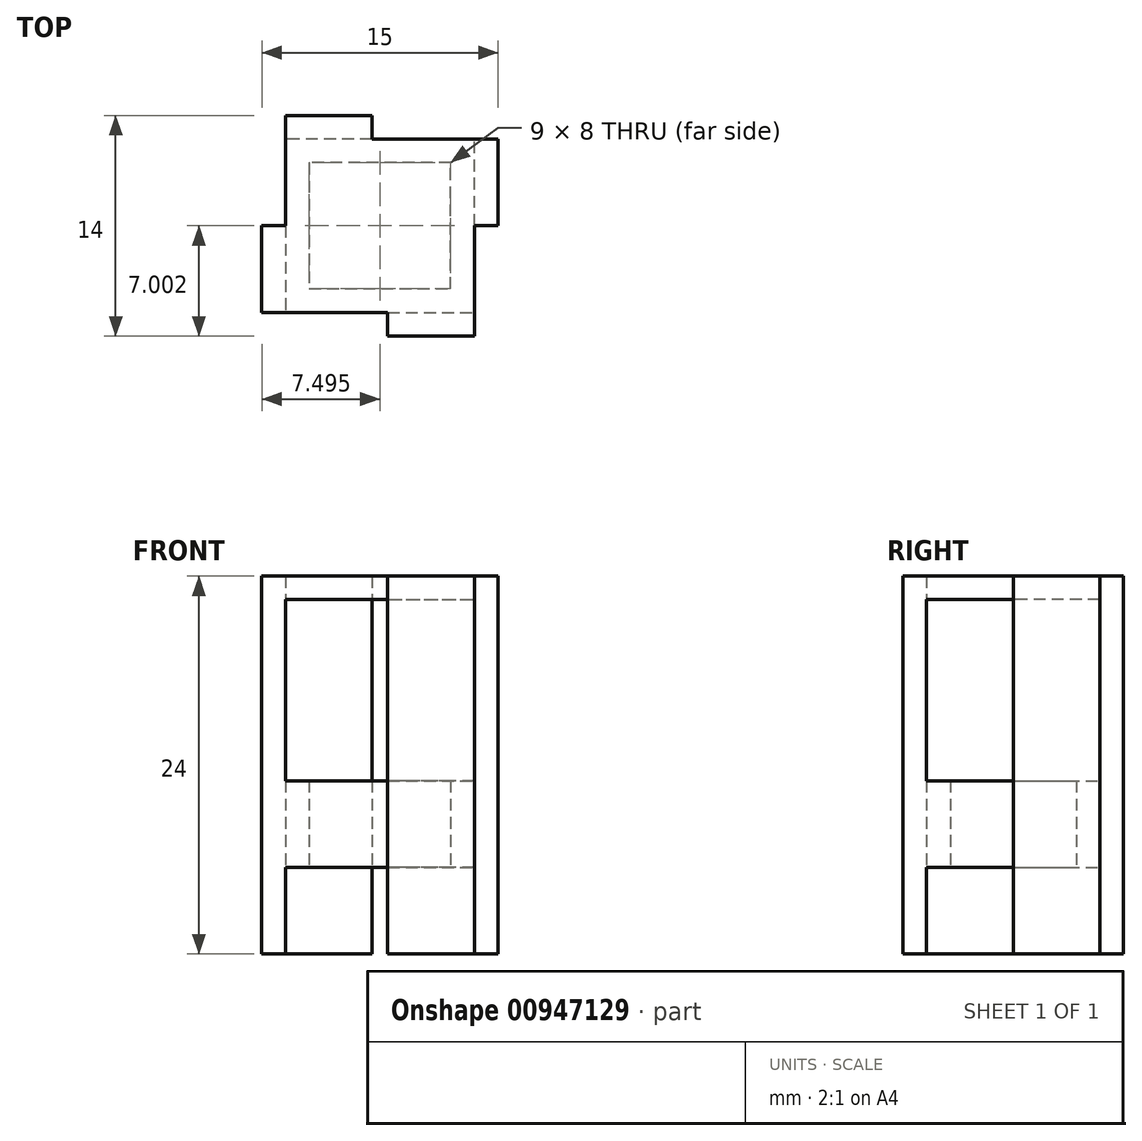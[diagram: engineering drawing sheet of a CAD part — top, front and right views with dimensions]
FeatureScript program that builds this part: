
annotation { "Feature Type Name" : "Feature", "Feature Type Description" : "" }
export const myFeature = defineFeature(function(context is Context, id is Id, definition is map)
    precondition{}
    {
        {
            var Q0;
            Q0=qCreatedBy(makeId("Top.planeOp"),FACE);
            var sketch = newSketch(context, id + "F0", { "sketchPlane" : qUnion([Q0])});
            skLineSegment(sketch, "E0.bottom", {"start": v(8.63, 13.95) * mm, "end": v(20.63, 13.95) * mm});
            skLineSegment(sketch, "E0.top", {"start": v(8.63, 8.45) * mm, "end": v(20.63, 8.45) * mm});
            skLineSegment(sketch, "E0.left", {"start": v(8.63, 13.95) * mm, "end": v(8.63, 8.45) * mm});
            skLineSegment(sketch, "E0.right", {"start": v(20.63, 13.95) * mm, "end": v(20.63, 8.45) * mm});
            skLineSegment(sketch, "E1.top", {"start": v(8.63, 2.95) * mm, "end": v(20.63, 2.95) * mm});
            skLineSegment(sketch, "E1.left", {"start": v(8.63, 8.45) * mm, "end": v(8.63, 2.95) * mm});
            skLineSegment(sketch, "E1.right", {"start": v(20.63, 8.45) * mm, "end": v(20.63, 2.95) * mm});
            skSolve(sketch);
        }
        {
            var Q0;
            Q0 = qSketchRegion(id + "F0", true);
            extrude(context, id + "F1", {"entities" : qUnion([Q0]), "depth" : 1.5 * mm, "offsetDistance" : 25 * mm});
        }
        {
            var Q0;
            Q0=makeQuery(id+"F1.opExtrude","SWEPT_FACE",FACE,{"disambiguationData":[OSD([sQuery(id+"F0.wireOp",EDGE,"E1.top")])]});
            var sketch = newSketch(context, id + "F2", { "sketchPlane" : qUnion([Q0])});
            skLineSegment(sketch, "E2.bottom", {"start": v(20.63, 1.5) * mm, "end": v(15.13, 1.5) * mm});
            skLineSegment(sketch, "E2.top", {"start": v(20.63, -22.5) * mm, "end": v(15.13, -22.5) * mm});
            skLineSegment(sketch, "E2.left", {"start": v(20.63, 1.5) * mm, "end": v(20.63, -22.5) * mm});
            skLineSegment(sketch, "E2.right", {"start": v(15.13, 1.5) * mm, "end": v(15.13, -22.5) * mm});
            skSolve(sketch);
        }
        {
            var Q0;
            Q0 = qSketchRegion(id + "F2", true);
            extrude(context, id + "F3", {"entities" : qUnion([Q0]), "operationType" : NewBodyOperationType.ADD, "depth" : 1.5 * mm, "offsetDistance" : 25 * mm});
        }
        {
            var Q0;
            Q0=makeQuery(id+"F1.opExtrude","SWEPT_FACE",FACE,{"disambiguationData":[OSD([sQuery(id+"F0.wireOp",EDGE,"E0.left"),sQuery(id+"F0.wireOp",EDGE,"E1.left")])]});
            var sketch = newSketch(context, id + "F4", { "sketchPlane" : qUnion([Q0])});
            skLineSegment(sketch, "E3.bottom", {"start": v(-2.95, 1.5) * mm, "end": v(-8.45, 1.5) * mm});
            skLineSegment(sketch, "E3.top", {"start": v(-2.95, -22.5) * mm, "end": v(-8.45, -22.5) * mm});
            skLineSegment(sketch, "E3.left", {"start": v(-2.95, 1.5) * mm, "end": v(-2.95, -22.5) * mm});
            skLineSegment(sketch, "E3.right", {"start": v(-8.45, 1.5) * mm, "end": v(-8.45, -22.5) * mm});
            skSolve(sketch);
        }
        {
            var Q0;
            {var subQ0=sQuery(id+"F4.wireOp",EDGE,"E3.top");Q0=makeQuery(id+"F4.imprint","IMPRINT",FACE,{"disambiguationData":[TD([[makeQuery(id+"F4.imprint","IMPRINT",EDGE,{"derivedFrom":subQ0}),-1.0]])]});}
            var Q1;
            {var subQ0=sQuery(id+"F4.wireOp",EDGE,"E3.bottom");Q1=makeQuery(id+"F4.imprint","IMPRINT",FACE,{"disambiguationData":[TD([[makeQuery(id+"F4.imprint","IMPRINT",EDGE,{"derivedFrom":subQ0}),-1.0]])]});}
            extrude(context, id + "F5", {"entities" : qUnion([Q0, Q1]), "operationType" : NewBodyOperationType.ADD, "depth" : 1.5 * mm, "offsetDistance" : 25 * mm});
        }
        {
            var Q0;
            Q0=makeQuery(id+"F1.opExtrude","SWEPT_FACE",FACE,{"disambiguationData":[OSD([sQuery(id+"F0.wireOp",EDGE,"E0.bottom")])]});
            var sketch = newSketch(context, id + "F6", { "sketchPlane" : qUnion([Q0])});
            skLineSegment(sketch, "E4.bottom", {"start": v(-8.63, 1.5) * mm, "end": v(-14.13, 1.5) * mm});
            skLineSegment(sketch, "E4.top", {"start": v(-8.63, -22.5) * mm, "end": v(-14.13, -22.5) * mm});
            skLineSegment(sketch, "E4.left", {"start": v(-8.63, 1.5) * mm, "end": v(-8.63, -22.5) * mm});
            skLineSegment(sketch, "E4.right", {"start": v(-14.13, 1.5) * mm, "end": v(-14.13, -22.5) * mm});
            skSolve(sketch);
        }
        {
            var Q0;
            Q0 = qSketchRegion(id + "F6", true);
            extrude(context, id + "F7", {"entities" : qUnion([Q0]), "operationType" : NewBodyOperationType.ADD, "depth" : 1.5 * mm, "offsetDistance" : 25 * mm});
        }
        {
            var Q0;
            Q0=makeQuery(id+"F3.boolean.opBoolean","MERGE",FACE,{"derivedFrom":[makeQuery(id+"F1.opExtrude","SWEPT_FACE",FACE,{"disambiguationData":[OSD([sQuery(id+"F0.wireOp",EDGE,"E0.right"),sQuery(id+"F0.wireOp",EDGE,"E1.right")])]}),makeQuery(id+"F3.opExtrude","SWEPT_FACE",FACE,{"disambiguationData":[OSD([sQuery(id+"F2.wireOp",EDGE,"E2.left")])]})]});
            var sketch = newSketch(context, id + "F8", { "sketchPlane" : qUnion([Q0])});
            skLineSegment(sketch, "E5.bottom", {"start": v(13.95, 1.5) * mm, "end": v(8.45, 1.5) * mm});
            skLineSegment(sketch, "E5.top", {"start": v(13.95, -22.5) * mm, "end": v(8.45, -22.5) * mm});
            skLineSegment(sketch, "E5.left", {"start": v(13.95, 1.5) * mm, "end": v(13.95, -22.5) * mm});
            skLineSegment(sketch, "E5.right", {"start": v(8.45, 1.5) * mm, "end": v(8.45, -22.5) * mm});
            skSolve(sketch);
        }
        {
            var Q0;
            Q0 = qSketchRegion(id + "F8", true);
            extrude(context, id + "F9", {"entities" : qUnion([Q0]), "operationType" : NewBodyOperationType.ADD, "depth" : 1.5 * mm, "offsetDistance" : 25 * mm});
        }
        {
            var Q0;
            Q0=makeQuery(id+"F7.boolean.opBoolean","MERGE",FACE,{"derivedFrom":[makeQuery(id+"F1.opExtrude","SWEPT_FACE",FACE,{"disambiguationData":[OSD([sQuery(id+"F0.wireOp",EDGE,"E0.left"),sQuery(id+"F0.wireOp",EDGE,"E1.left")])]}),makeQuery(id+"F7.opExtrude","SWEPT_FACE",FACE,{"disambiguationData":[OSD([sQuery(id+"F6.wireOp",EDGE,"E4.left")])]})]});
            var sketch = newSketch(context, id + "F10", { "sketchPlane" : qUnion([Q0])});
            skLineSegment(sketch, "E6.bottom", {"start": v(-13.95, -11.5) * mm, "end": v(-4.45, -11.5) * mm});
            skLineSegment(sketch, "E6.top", {"start": v(-13.95, -17) * mm, "end": v(-4.45, -17) * mm});
            skLineSegment(sketch, "E6.left", {"start": v(-13.95, -11.5) * mm, "end": v(-13.95, -17) * mm});
            skLineSegment(sketch, "E6.right", {"start": v(-4.45, -11.5) * mm, "end": v(-4.45, -17) * mm});
            skSolve(sketch);
        }
        {
            var Q0;
            Q0=makeQuery(id+"F10.imprint","IMPRINT",FACE,{"disambiguationData":[TD([[makeQuery(id+"F10.imprint","IMPRINT",EDGE,{"derivedFrom":sQuery(id+"F10.wireOp",EDGE,"E6.bottom")}),-1.0]])]});
            extrude(context, id + "F11", {"entities" : qUnion([Q0]), "operationType" : NewBodyOperationType.ADD, "oppositeDirection" : true, "depth" : 1.5 * mm, "offsetDistance" : 25 * mm});
        }
        {
            var Q0;
            Q0=makeQuery(id+"F9.boolean.opBoolean","MERGE",FACE,{"derivedFrom":[makeQuery(id+"F1.opExtrude","SWEPT_FACE",FACE,{"disambiguationData":[OSD([sQuery(id+"F0.wireOp",EDGE,"E0.bottom")])]}),makeQuery(id+"F9.opExtrude","SWEPT_FACE",FACE,{"disambiguationData":[OSD([sQuery(id+"F8.wireOp",EDGE,"E5.left")])]})]});
            var sketch = newSketch(context, id + "F12", { "sketchPlane" : qUnion([Q0])});
            skLineSegment(sketch, "E7.bottom", {"start": v(-20.63, -11.5) * mm, "end": v(-10.13, -11.5) * mm});
            skLineSegment(sketch, "E7.top", {"start": v(-20.63, -17) * mm, "end": v(-10.13, -17) * mm});
            skLineSegment(sketch, "E7.left", {"start": v(-20.63, -11.5) * mm, "end": v(-20.63, -17) * mm});
            skLineSegment(sketch, "E7.right", {"start": v(-10.13, -11.5) * mm, "end": v(-10.13, -17) * mm});
            skSolve(sketch);
        }
        {
            var Q0;
            Q0=makeQuery(id+"F12.imprint","IMPRINT",FACE,{"disambiguationData":[TD([[makeQuery(id+"F12.imprint","IMPRINT",EDGE,{"derivedFrom":sQuery(id+"F12.wireOp",EDGE,"E7.bottom")}),-1.0]])]});
            extrude(context, id + "F13", {"entities" : qUnion([Q0]), "operationType" : NewBodyOperationType.ADD, "oppositeDirection" : true, "depth" : 1.5 * mm, "offsetDistance" : 25 * mm});
        }
        {
            var Q0;
            Q0=makeQuery(id+"F3.boolean.opBoolean","MERGE",FACE,{"derivedFrom":[makeQuery(id+"F1.opExtrude","SWEPT_FACE",FACE,{"disambiguationData":[OSD([sQuery(id+"F0.wireOp",EDGE,"E0.right"),sQuery(id+"F0.wireOp",EDGE,"E1.right")])]}),makeQuery(id+"F3.opExtrude","SWEPT_FACE",FACE,{"disambiguationData":[OSD([sQuery(id+"F2.wireOp",EDGE,"E2.left")])]})]});
            var sketch = newSketch(context, id + "F14", { "sketchPlane" : qUnion([Q0])});
            skLineSegment(sketch, "E8.bottom", {"start": v(2.95, -11.5) * mm, "end": v(12.45, -11.5) * mm});
            skLineSegment(sketch, "E8.top", {"start": v(2.95, -17) * mm, "end": v(12.45, -17) * mm});
            skLineSegment(sketch, "E8.left", {"start": v(2.95, -11.5) * mm, "end": v(2.95, -17) * mm});
            skLineSegment(sketch, "E8.right", {"start": v(12.45, -11.5) * mm, "end": v(12.45, -17) * mm});
            skSolve(sketch);
        }
        {
            var Q0;
            Q0=makeQuery(id+"F14.imprint","IMPRINT",FACE,{"disambiguationData":[TD([[makeQuery(id+"F14.imprint","IMPRINT",EDGE,{"derivedFrom":sQuery(id+"F14.wireOp",EDGE,"E8.bottom")}),-1.0]])]});
            extrude(context, id + "F15", {"entities" : qUnion([Q0]), "operationType" : NewBodyOperationType.ADD, "oppositeDirection" : true, "depth" : 1.5 * mm, "offsetDistance" : 25 * mm});
        }
        {
            var Q0;
            Q0=makeQuery(id+"F5.boolean.opBoolean","MERGE",FACE,{"derivedFrom":[makeQuery(id+"F1.opExtrude","SWEPT_FACE",FACE,{"disambiguationData":[OSD([sQuery(id+"F0.wireOp",EDGE,"E1.top")])]}),makeQuery(id+"F5.opExtrude","SWEPT_FACE",FACE,{"disambiguationData":[OSD([sQuery(id+"F4.wireOp",EDGE,"E3.left")])]})]});
            var sketch = newSketch(context, id + "F16", { "sketchPlane" : qUnion([Q0])});
            skLineSegment(sketch, "E9.bottom", {"start": v(8.63, -11.5) * mm, "end": v(19.13, -11.5) * mm});
            skLineSegment(sketch, "E9.top", {"start": v(8.63, -17) * mm, "end": v(19.13, -17) * mm});
            skLineSegment(sketch, "E9.left", {"start": v(8.63, -11.5) * mm, "end": v(8.63, -17) * mm});
            skLineSegment(sketch, "E9.right", {"start": v(19.13, -11.5) * mm, "end": v(19.13, -17) * mm});
            skSolve(sketch);
        }
        {
            var Q0;
            Q0 = qSketchRegion(id + "F16", true);
            extrude(context, id + "F17", {"entities" : qUnion([Q0]), "operationType" : NewBodyOperationType.ADD, "oppositeDirection" : true, "depth" : 1.5 * mm, "offsetDistance" : 25 * mm});
        }
    });
